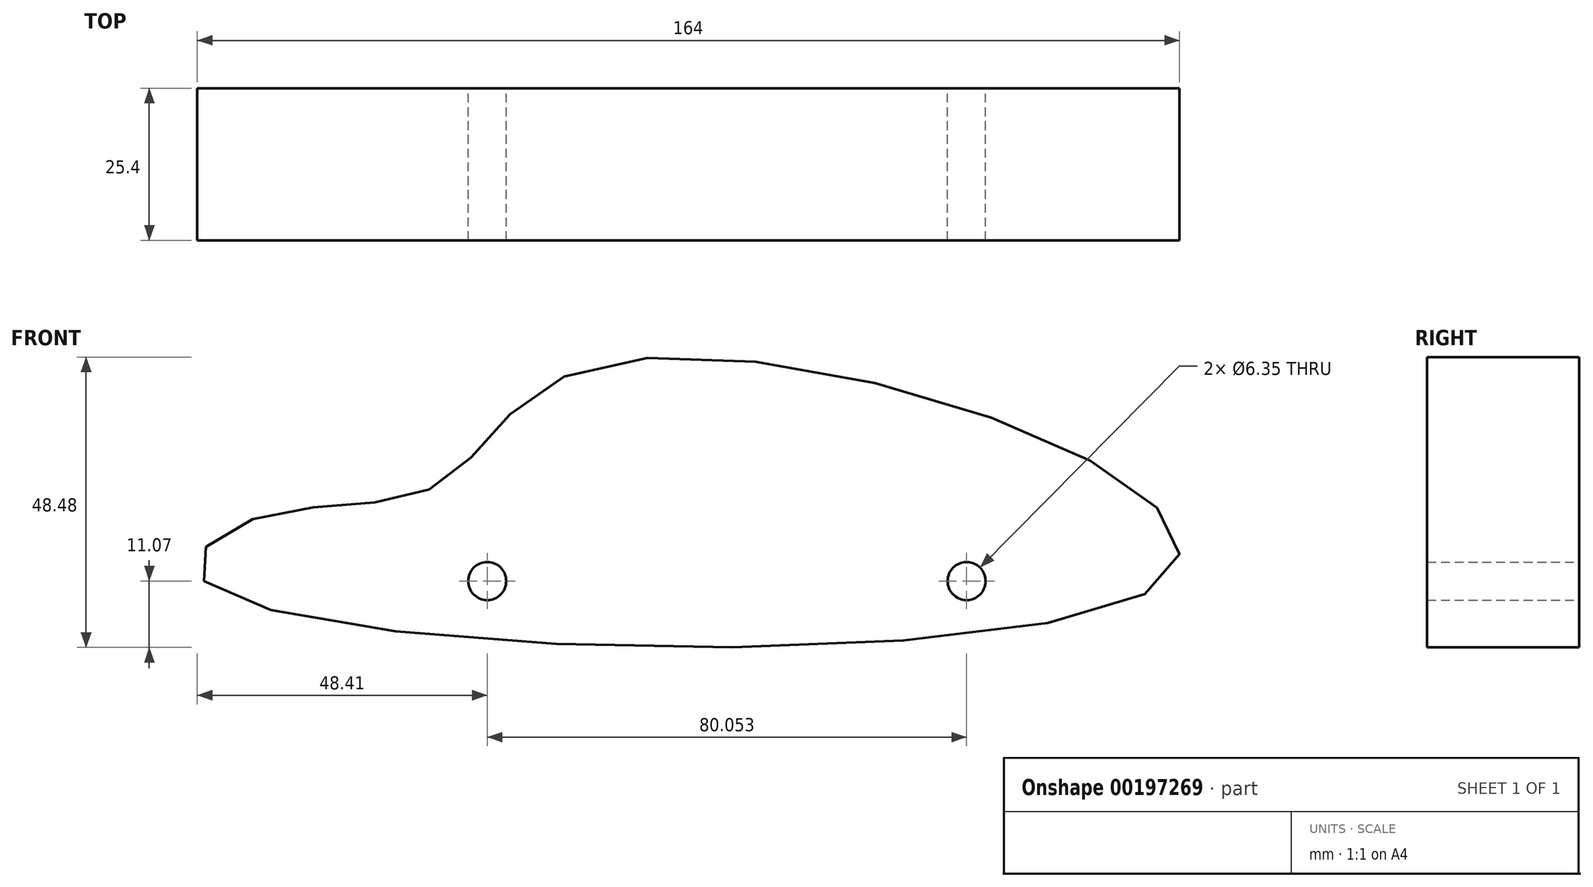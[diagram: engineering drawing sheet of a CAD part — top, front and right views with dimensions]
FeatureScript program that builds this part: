
annotation { "Feature Type Name" : "Feature", "Feature Type Description" : "" }
export const myFeature = defineFeature(function(context is Context, id is Id, definition is map)
    precondition{}
    {
        {
            var Q0;
            Q0=qCreatedBy(makeId("Front.planeOp"),FACE);
            var sketch = newSketch(context, id + "F0", { "sketchPlane" : qUnion([Q0])});
            skFitSpline(sketch, "E0", {"points": [v(-63.4, 0) * mm, v(-54.68, 10.53) * mm, v(-24.68, 15.85) * mm, v(0, 35.43) * mm, v(93.4, 14.36) * mm, v(93.62, -2.23) * mm, v(-63.4, 0) * mm]});
            skSolve(sketch);
        }
        {
            var Q0;
            Q0=makeQuery(id+"F0.imprint","IMPRINT",FACE,{"disambiguationData":[TD([[makeQuery(id+"F0.imprint","IMPRINT",EDGE,{"derivedFrom":sQuery(id+"F0.wireOp",EDGE,"E0")}),-1.0]])]});
            extrude(context, id + "F1", {"entities" : qUnion([Q0]), "depth" : 25.4 * mm});
        }
        {
            var Q0;
            Q0=qCreatedBy(makeId("Front.planeOp"),FACE);
            var sketch = newSketch(context, id + "F2", { "sketchPlane" : qUnion([Q0])});
            skCircle(sketch, "E1", {"center": v(-31.97, 0) * mm, "radius": 3.17 * mm});
            skCircle(sketch, "E2", {"center": v(63.93, 0) * mm, "radius": 3.18 * mm});
            skSolve(sketch);
        }
        {
            var Q0;
            Q0=sQuery(id+"F2.wireOp",VERTEX,"E2.center");
            var Q1;
            Q1=makeQuery(id+"F1.opExtrude","SWEPT_BODY",BODY,{"disambiguationData":[OSD([sQuery(id+"F0.wireOp",EDGE,"E0")])]});
            hole(context, id + "F3", {"style" : HoleStyle.SIMPLE, "endStyle" : HoleEndStyle.THROUGH, "oppositeDirection" : true, "holeDiameter" : 6.35 * mm, "locations" : qUnion([Q0]), "scope" : qUnion([Q1]), "isTappedThrough" : true});
        }
        {
            var Q0;
            Q0=qCreatedBy(makeId("Front.planeOp"),FACE);
            var sketch = newSketch(context, id + "F4", { "sketchPlane" : qUnion([Q0])});
            skCircle(sketch, "E3", {"center": v(-16.12, 0) * mm, "radius": 3.18 * mm});
            skSolve(sketch);
        }
        {
            var Q0;
            Q0=sQuery(id+"F4.wireOp",VERTEX,"E3.center");
            var Q1;
            Q1=makeQuery(id+"F1.opExtrude","SWEPT_BODY",BODY,{"disambiguationData":[OSD([sQuery(id+"F0.wireOp",EDGE,"E0")])]});
            hole(context, id + "F5", {"style" : HoleStyle.SIMPLE, "endStyle" : HoleEndStyle.THROUGH, "oppositeDirection" : true, "holeDiameter" : 6.35 * mm, "locations" : qUnion([Q0]), "scope" : qUnion([Q1]), "isTappedThrough" : true});
        }
    });
